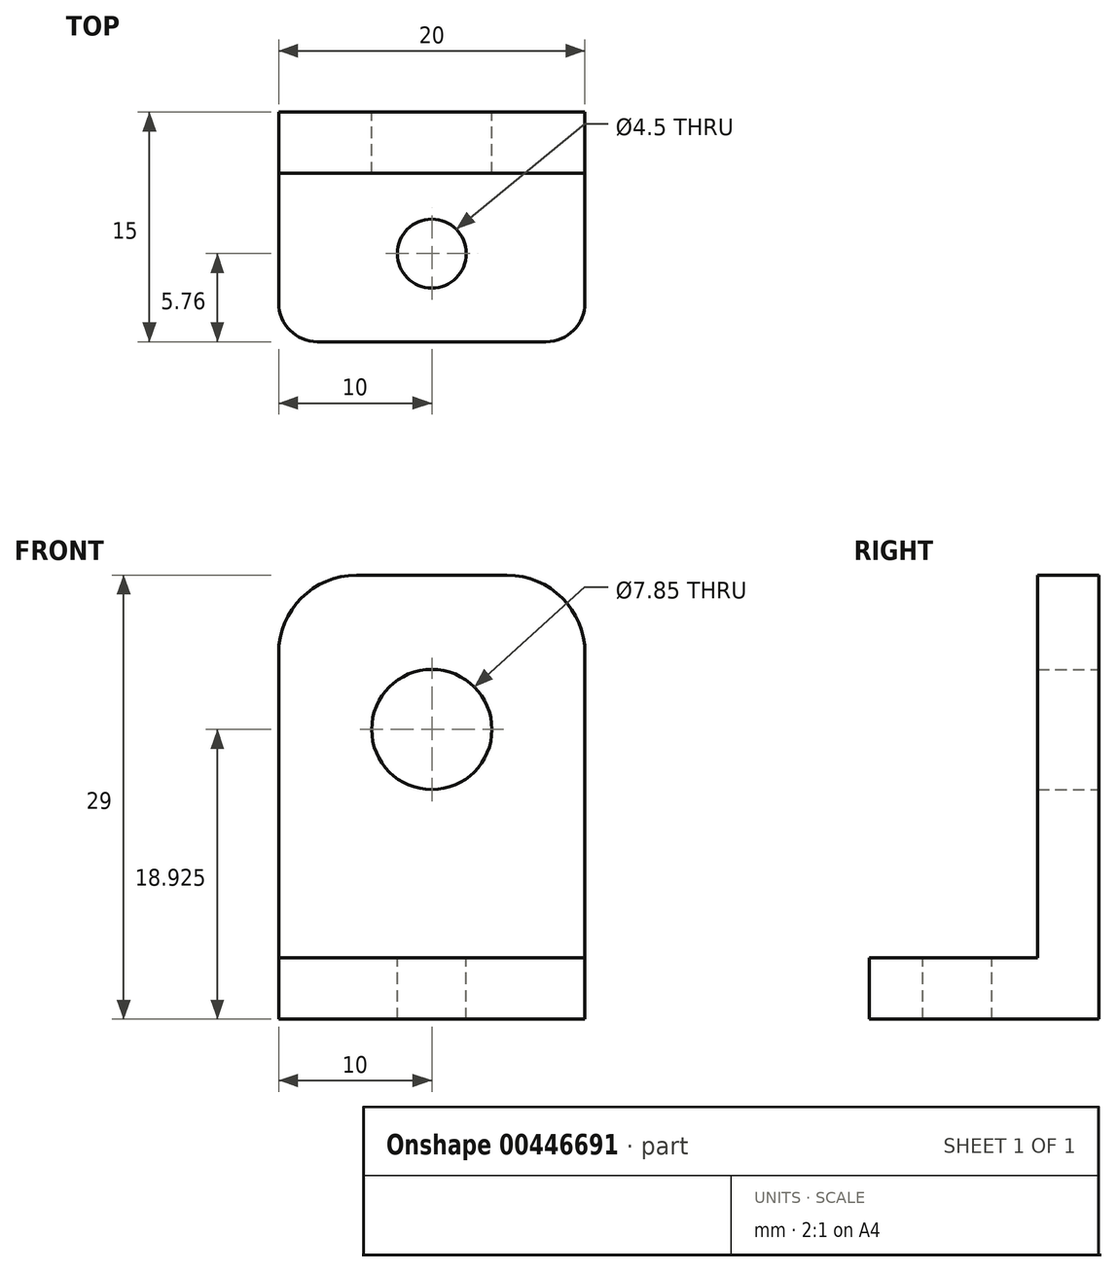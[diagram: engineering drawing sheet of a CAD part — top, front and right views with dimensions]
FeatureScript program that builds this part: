
annotation { "Feature Type Name" : "Feature", "Feature Type Description" : "" }
export const myFeature = defineFeature(function(context is Context, id is Id, definition is map)
    precondition{}
    {
        {
            var Q0;
            Q0=qCreatedBy(makeId("Top.planeOp"),FACE);
            var sketch = newSketch(context, id + "F0", { "sketchPlane" : qUnion([Q0])});
            skLineSegment(sketch, "E0.bottom", {"start": v(0, 0) * mm, "end": v(20, 0) * mm});
            skLineSegment(sketch, "E0.top", {"start": v(0, 15) * mm, "end": v(20, 15) * mm});
            skLineSegment(sketch, "E0.left", {"start": v(0, 0) * mm, "end": v(0, 15) * mm});
            skLineSegment(sketch, "E0.right", {"start": v(20, 0) * mm, "end": v(20, 15) * mm});
            skSolve(sketch);
        }
        {
            var Q0;
            Q0 = qSketchRegion(id + "F0", true);
            extrude(context, id + "F1", {"entities" : qUnion([Q0]), "depth" : 4 * mm});
        }
        {
            var Q0;
            Q0=makeQuery(id+"F1.opExtrude","CAP_FACE",FACE,{"disambiguationData":[OSD([sQuery(id+"F0.wireOp",EDGE,"E0.bottom"),sQuery(id+"F0.wireOp",EDGE,"E0.top"),sQuery(id+"F0.wireOp",EDGE,"E0.left"),sQuery(id+"F0.wireOp",EDGE,"E0.right")])],"isStart":false});
            var sketch = newSketch(context, id + "F2", { "sketchPlane" : qUnion([Q0])});
            skLineSegment(sketch, "E1.bottom", {"start": v(0, 15) * mm, "end": v(20, 15) * mm});
            skLineSegment(sketch, "E1.top", {"start": v(0, 11) * mm, "end": v(20, 11) * mm});
            skLineSegment(sketch, "E1.left", {"start": v(0, 15) * mm, "end": v(0, 11) * mm});
            skLineSegment(sketch, "E1.right", {"start": v(20, 15) * mm, "end": v(20, 11) * mm});
            skSolve(sketch);
        }
        {
            var Q0;
            Q0 = qSketchRegion(id + "F2", true);
            extrude(context, id + "F3", {"entities" : qUnion([Q0]), "operationType" : NewBodyOperationType.ADD, "depth" : 25 * mm});
        }
        {
            var Q0;
            Q0=makeQuery(id+"F1.opExtrude","CAP_FACE",FACE,{"disambiguationData":[OSD([sQuery(id+"F0.wireOp",EDGE,"E0.bottom"),sQuery(id+"F0.wireOp",EDGE,"E0.top"),sQuery(id+"F0.wireOp",EDGE,"E0.left"),sQuery(id+"F0.wireOp",EDGE,"E0.right")])],"isStart":false});
            var sketch = newSketch(context, id + "F4", { "sketchPlane" : qUnion([Q0])});
            skCircle(sketch, "E2", {"center": v(10, 5.76) * mm, "radius": 2.25 * mm});
            skPoint(sketch, "E2.centerSnap0", {"position": v(10, 0) * mm});
            skSolve(sketch);
        }
        {
            var Q0;
            Q0 = qSketchRegion(id + "F4", true);
            extrude(context, id + "F5", {"entities" : qUnion([Q0]), "operationType" : NewBodyOperationType.REMOVE, "oppositeDirection" : true, "depth" : 25.4 * mm});
        }
        {
            var Q0;
            Q0=makeQuery(id+"F3.boolean.opBoolean","MERGE",FACE,{"derivedFrom":[makeQuery(id+"F1.opExtrude","SWEPT_FACE",FACE,{"disambiguationData":[OSD([sQuery(id+"F0.wireOp",EDGE,"E0.top")])]}),makeQuery(id+"F3.opExtrude","SWEPT_FACE",FACE,{"disambiguationData":[OSD([sQuery(id+"F2.wireOp",EDGE,"E1.bottom")])]})]});
            var sketch = newSketch(context, id + "F6", { "sketchPlane" : qUnion([Q0])});
            skCircle(sketch, "E3", {"center": v(-10, 18.92) * mm, "radius": 3.92 * mm});
            skPoint(sketch, "E3.centerSnap0", {"position": v(-10, 0) * mm});
            skSolve(sketch);
        }
        {
            var Q0;
            Q0 = qSketchRegion(id + "F6", true);
            extrude(context, id + "F7", {"entities" : qUnion([Q0]), "operationType" : NewBodyOperationType.REMOVE, "oppositeDirection" : true, "depth" : 25.4 * mm});
        }
        {
            var Q0;
            Q0=makeQuery(id+"F1.opExtrude","SWEPT_EDGE",EDGE,{"disambiguationData":[OSD([sQuery(id+"F0.wireOp",EDGE,"E0.bottom"),sQuery(id+"F0.wireOp",EDGE,"E0.right")])]});
            var Q1;
            Q1=makeQuery(id+"F1.opExtrude","SWEPT_EDGE",EDGE,{"disambiguationData":[OSD([sQuery(id+"F0.wireOp",EDGE,"E0.bottom"),sQuery(id+"F0.wireOp",EDGE,"E0.left")])]});
            fillet(context, id + "F8", {"entities" : qUnion([Q0, Q1]), "radius" : 2.54 * mm, "tangentPropagation" : true, "allowEdgeOverflow" : false});
        }
        {
            var Q0;
            Q0=makeQuery(id+"F3.opExtrude","CAP_EDGE",EDGE,{"disambiguationData":[OSD([sQuery(id+"F2.wireOp",EDGE,"E1.right")])],"isStart":false});
            var Q1;
            Q1=makeQuery(id+"F3.opExtrude","CAP_EDGE",EDGE,{"disambiguationData":[OSD([sQuery(id+"F2.wireOp",EDGE,"E1.left")])],"isStart":false});
            fillet(context, id + "F9", {"entities" : qUnion([Q0, Q1]), "radius" : 5.08 * mm, "tangentPropagation" : true, "allowEdgeOverflow" : false});
        }
    });
